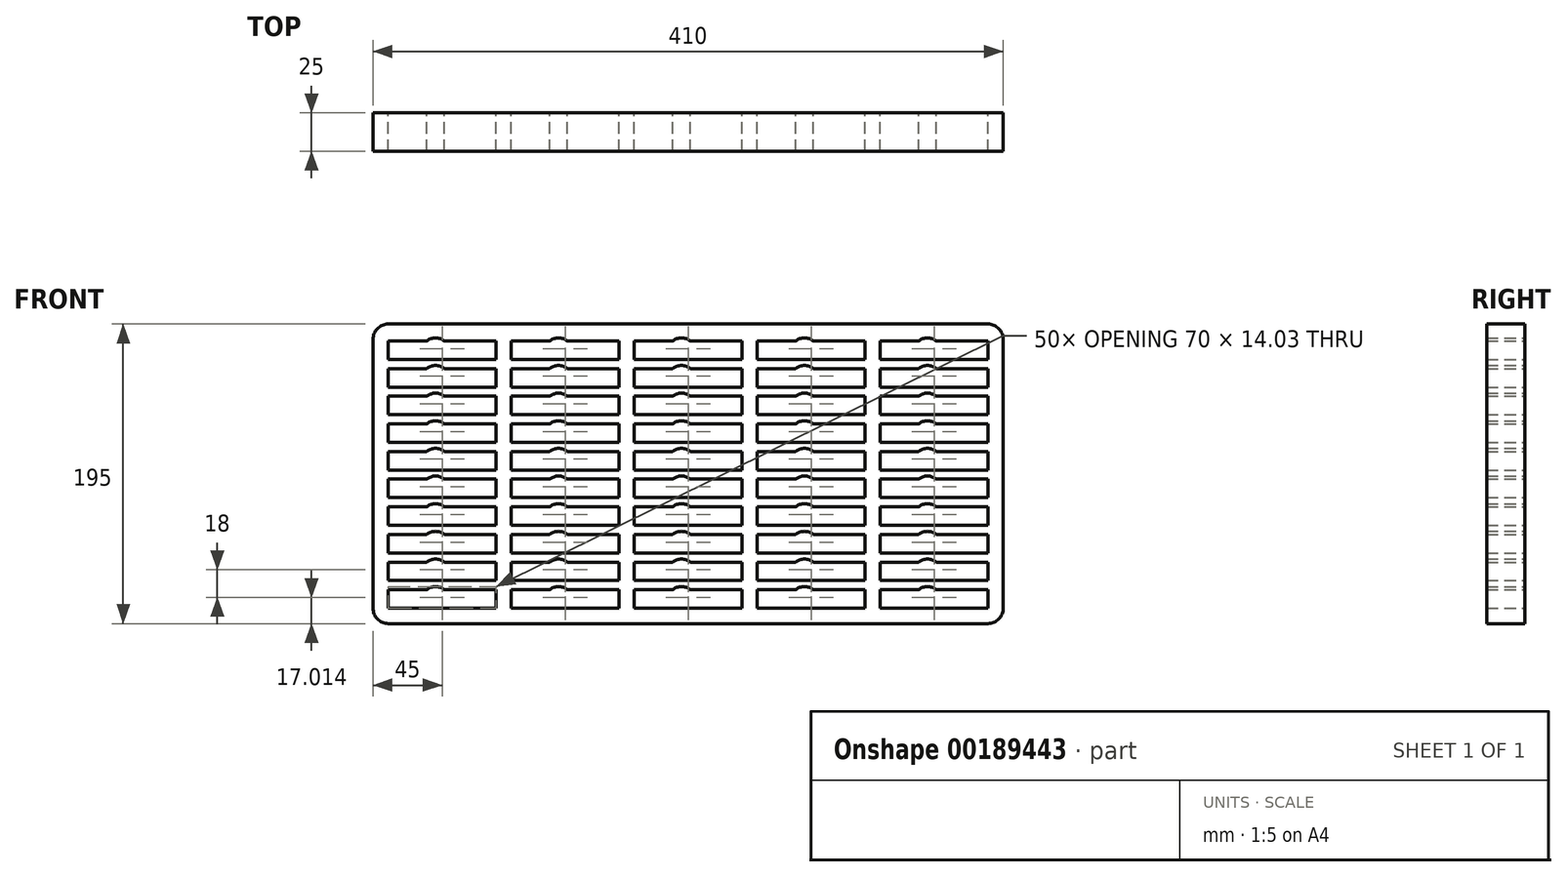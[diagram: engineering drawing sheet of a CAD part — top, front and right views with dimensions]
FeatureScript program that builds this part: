
annotation { "Feature Type Name" : "Feature", "Feature Type Description" : "" }
export const myFeature = defineFeature(function(context is Context, id is Id, definition is map)
    precondition{}
    {
        {
            var Q0;
            Q0=qCreatedBy(makeId("Front.planeOp"),FACE);
            var sketch = newSketch(context, id + "F0", { "sketchPlane" : qUnion([Q0])});
            skLineSegment(sketch, "E0.bottom", {"start": v(10, 0) * mm, "end": v(400, 0) * mm});
            skLineSegment(sketch, "E0.top", {"start": v(10, 195) * mm, "end": v(400, 195) * mm});
            skLineSegment(sketch, "E0.left", {"start": v(0, 10) * mm, "end": v(0, 185) * mm});
            skLineSegment(sketch, "E0.right", {"start": v(410, 10) * mm, "end": v(410, 185) * mm});
            skLineSegment(sketch, "E1.bottom", {"start": v(10, 10) * mm, "end": v(80, 10) * mm});
            skLineSegment(sketch, "E1.top", {"start": v(10, 22) * mm, "end": v(80, 22) * mm});
            skLineSegment(sketch, "E1.left", {"start": v(10, 10) * mm, "end": v(10, 22) * mm});
            skLineSegment(sketch, "E1.right", {"start": v(80, 10) * mm, "end": v(80, 22) * mm});
            skArc(sketch, "E2", {"start": v(46.47, 22) * mm, "mid": v(40.7, 24.03) * mm, "end": v(34.93, 22) * mm});
            skLineSegment(sketch, "E3.0.1.0", {"start": v(10, 28) * mm, "end": v(80, 28) * mm});
            skLineSegment(sketch, "E3.0.1.1", {"start": v(80, 28) * mm, "end": v(80, 40) * mm});
            skLineSegment(sketch, "E3.0.1.2", {"start": v(10, 40) * mm, "end": v(80, 40) * mm});
            skArc(sketch, "E3.0.1.3", {"start": v(46.47, 40) * mm, "mid": v(40.7, 42.03) * mm, "end": v(34.93, 40) * mm});
            skLineSegment(sketch, "E3.0.1.4", {"start": v(10, 28) * mm, "end": v(10, 40) * mm});
            skLineSegment(sketch, "E3.0.2.0", {"start": v(10, 46) * mm, "end": v(80, 46) * mm});
            skLineSegment(sketch, "E3.0.2.1", {"start": v(80, 46) * mm, "end": v(80, 58) * mm});
            skLineSegment(sketch, "E3.0.2.2", {"start": v(10, 58) * mm, "end": v(80, 58) * mm});
            skArc(sketch, "E3.0.2.3", {"start": v(46.47, 58) * mm, "mid": v(40.7, 60.03) * mm, "end": v(34.93, 58) * mm});
            skLineSegment(sketch, "E3.0.2.4", {"start": v(10, 46) * mm, "end": v(10, 58) * mm});
            skLineSegment(sketch, "E3.0.3.0", {"start": v(10, 64) * mm, "end": v(80, 64) * mm});
            skLineSegment(sketch, "E3.0.3.1", {"start": v(80, 64) * mm, "end": v(80, 76) * mm});
            skLineSegment(sketch, "E3.0.3.2", {"start": v(10, 76) * mm, "end": v(80, 76) * mm});
            skArc(sketch, "E3.0.3.3", {"start": v(46.47, 76) * mm, "mid": v(40.7, 78.03) * mm, "end": v(34.93, 76) * mm});
            skLineSegment(sketch, "E3.0.3.4", {"start": v(10, 64) * mm, "end": v(10, 76) * mm});
            skLineSegment(sketch, "E3.0.4.0", {"start": v(10, 82) * mm, "end": v(80, 82) * mm});
            skLineSegment(sketch, "E3.0.4.1", {"start": v(80, 82) * mm, "end": v(80, 94) * mm});
            skLineSegment(sketch, "E3.0.4.2", {"start": v(10, 94) * mm, "end": v(80, 94) * mm});
            skArc(sketch, "E3.0.4.3", {"start": v(46.47, 94) * mm, "mid": v(40.7, 96.03) * mm, "end": v(34.93, 94) * mm});
            skLineSegment(sketch, "E3.0.4.4", {"start": v(10, 82) * mm, "end": v(10, 94) * mm});
            skLineSegment(sketch, "E3.0.5.0", {"start": v(10, 100) * mm, "end": v(80, 100) * mm});
            skLineSegment(sketch, "E3.0.5.1", {"start": v(80, 100) * mm, "end": v(80, 112) * mm});
            skLineSegment(sketch, "E3.0.5.2", {"start": v(10, 112) * mm, "end": v(80, 112) * mm});
            skArc(sketch, "E3.0.5.3", {"start": v(46.47, 112) * mm, "mid": v(40.7, 114.03) * mm, "end": v(34.93, 112) * mm});
            skLineSegment(sketch, "E3.0.5.4", {"start": v(10, 100) * mm, "end": v(10, 112) * mm});
            skLineSegment(sketch, "E3.0.6.0", {"start": v(10, 118) * mm, "end": v(80, 118) * mm});
            skLineSegment(sketch, "E3.0.6.1", {"start": v(80, 118) * mm, "end": v(80, 130) * mm});
            skLineSegment(sketch, "E3.0.6.2", {"start": v(10, 130) * mm, "end": v(80, 130) * mm});
            skArc(sketch, "E3.0.6.3", {"start": v(46.47, 130) * mm, "mid": v(40.7, 132.03) * mm, "end": v(34.93, 130) * mm});
            skLineSegment(sketch, "E3.0.6.4", {"start": v(10, 118) * mm, "end": v(10, 130) * mm});
            skLineSegment(sketch, "E3.0.7.0", {"start": v(10, 136) * mm, "end": v(80, 136) * mm});
            skLineSegment(sketch, "E3.0.7.1", {"start": v(80, 136) * mm, "end": v(80, 148) * mm});
            skLineSegment(sketch, "E3.0.7.2", {"start": v(10, 148) * mm, "end": v(80, 148) * mm});
            skArc(sketch, "E3.0.7.3", {"start": v(46.47, 148) * mm, "mid": v(40.7, 150.03) * mm, "end": v(34.93, 148) * mm});
            skLineSegment(sketch, "E3.0.7.4", {"start": v(10, 136) * mm, "end": v(10, 148) * mm});
            skLineSegment(sketch, "E3.0.8.0", {"start": v(10, 154) * mm, "end": v(80, 154) * mm});
            skLineSegment(sketch, "E3.0.8.1", {"start": v(80, 154) * mm, "end": v(80, 166) * mm});
            skLineSegment(sketch, "E3.0.8.2", {"start": v(10, 166) * mm, "end": v(80, 166) * mm});
            skArc(sketch, "E3.0.8.3", {"start": v(46.47, 166) * mm, "mid": v(40.7, 168.03) * mm, "end": v(34.93, 166) * mm});
            skLineSegment(sketch, "E3.0.8.4", {"start": v(10, 154) * mm, "end": v(10, 166) * mm});
            skLineSegment(sketch, "E3.0.9.0", {"start": v(10, 172) * mm, "end": v(80, 172) * mm});
            skLineSegment(sketch, "E3.0.9.1", {"start": v(80, 172) * mm, "end": v(80, 184) * mm});
            skLineSegment(sketch, "E3.0.9.2", {"start": v(10, 184) * mm, "end": v(80, 184) * mm});
            skArc(sketch, "E3.0.9.3", {"start": v(46.47, 184) * mm, "mid": v(40.7, 186.03) * mm, "end": v(34.93, 184) * mm});
            skLineSegment(sketch, "E3.0.9.4", {"start": v(10, 172) * mm, "end": v(10, 184) * mm});
            skLineSegment(sketch, "E3.1.0.0", {"start": v(90, 10) * mm, "end": v(160, 10) * mm});
            skLineSegment(sketch, "E3.1.0.1", {"start": v(160, 10) * mm, "end": v(160, 22) * mm});
            skLineSegment(sketch, "E3.1.0.2", {"start": v(90, 22) * mm, "end": v(160, 22) * mm});
            skArc(sketch, "E3.1.0.3", {"start": v(126.47, 22) * mm, "mid": v(120.7, 24.03) * mm, "end": v(114.93, 22) * mm});
            skLineSegment(sketch, "E3.1.0.4", {"start": v(90, 10) * mm, "end": v(90, 22) * mm});
            skLineSegment(sketch, "E3.1.1.0", {"start": v(90, 28) * mm, "end": v(160, 28) * mm});
            skLineSegment(sketch, "E3.1.1.1", {"start": v(160, 28) * mm, "end": v(160, 40) * mm});
            skLineSegment(sketch, "E3.1.1.2", {"start": v(90, 40) * mm, "end": v(160, 40) * mm});
            skArc(sketch, "E3.1.1.3", {"start": v(126.47, 40) * mm, "mid": v(120.7, 42.03) * mm, "end": v(114.93, 40) * mm});
            skLineSegment(sketch, "E3.1.1.4", {"start": v(90, 28) * mm, "end": v(90, 40) * mm});
            skLineSegment(sketch, "E3.1.2.0", {"start": v(90, 46) * mm, "end": v(160, 46) * mm});
            skLineSegment(sketch, "E3.1.2.1", {"start": v(160, 46) * mm, "end": v(160, 58) * mm});
            skLineSegment(sketch, "E3.1.2.2", {"start": v(90, 58) * mm, "end": v(160, 58) * mm});
            skArc(sketch, "E3.1.2.3", {"start": v(126.47, 58) * mm, "mid": v(120.7, 60.03) * mm, "end": v(114.93, 58) * mm});
            skLineSegment(sketch, "E3.1.2.4", {"start": v(90, 46) * mm, "end": v(90, 58) * mm});
            skLineSegment(sketch, "E3.1.3.0", {"start": v(90, 64) * mm, "end": v(160, 64) * mm});
            skLineSegment(sketch, "E3.1.3.1", {"start": v(160, 64) * mm, "end": v(160, 76) * mm});
            skLineSegment(sketch, "E3.1.3.2", {"start": v(90, 76) * mm, "end": v(160, 76) * mm});
            skArc(sketch, "E3.1.3.3", {"start": v(126.47, 76) * mm, "mid": v(120.7, 78.03) * mm, "end": v(114.93, 76) * mm});
            skLineSegment(sketch, "E3.1.3.4", {"start": v(90, 64) * mm, "end": v(90, 76) * mm});
            skLineSegment(sketch, "E3.1.4.0", {"start": v(90, 82) * mm, "end": v(160, 82) * mm});
            skLineSegment(sketch, "E3.1.4.1", {"start": v(160, 82) * mm, "end": v(160, 94) * mm});
            skLineSegment(sketch, "E3.1.4.2", {"start": v(90, 94) * mm, "end": v(160, 94) * mm});
            skArc(sketch, "E3.1.4.3", {"start": v(126.47, 94) * mm, "mid": v(120.7, 96.03) * mm, "end": v(114.93, 94) * mm});
            skLineSegment(sketch, "E3.1.4.4", {"start": v(90, 82) * mm, "end": v(90, 94) * mm});
            skLineSegment(sketch, "E3.1.5.0", {"start": v(90, 100) * mm, "end": v(160, 100) * mm});
            skLineSegment(sketch, "E3.1.5.1", {"start": v(160, 100) * mm, "end": v(160, 112) * mm});
            skLineSegment(sketch, "E3.1.5.2", {"start": v(90, 112) * mm, "end": v(160, 112) * mm});
            skArc(sketch, "E3.1.5.3", {"start": v(126.47, 112) * mm, "mid": v(120.7, 114.03) * mm, "end": v(114.93, 112) * mm});
            skLineSegment(sketch, "E3.1.5.4", {"start": v(90, 100) * mm, "end": v(90, 112) * mm});
            skLineSegment(sketch, "E3.1.6.0", {"start": v(90, 118) * mm, "end": v(160, 118) * mm});
            skLineSegment(sketch, "E3.1.6.1", {"start": v(160, 118) * mm, "end": v(160, 130) * mm});
            skLineSegment(sketch, "E3.1.6.2", {"start": v(90, 130) * mm, "end": v(160, 130) * mm});
            skArc(sketch, "E3.1.6.3", {"start": v(126.47, 130) * mm, "mid": v(120.7, 132.03) * mm, "end": v(114.93, 130) * mm});
            skLineSegment(sketch, "E3.1.6.4", {"start": v(90, 118) * mm, "end": v(90, 130) * mm});
            skLineSegment(sketch, "E3.1.7.0", {"start": v(90, 136) * mm, "end": v(160, 136) * mm});
            skLineSegment(sketch, "E3.1.7.1", {"start": v(160, 136) * mm, "end": v(160, 148) * mm});
            skLineSegment(sketch, "E3.1.7.2", {"start": v(90, 148) * mm, "end": v(160, 148) * mm});
            skArc(sketch, "E3.1.7.3", {"start": v(126.47, 148) * mm, "mid": v(120.7, 150.03) * mm, "end": v(114.93, 148) * mm});
            skLineSegment(sketch, "E3.1.7.4", {"start": v(90, 136) * mm, "end": v(90, 148) * mm});
            skLineSegment(sketch, "E3.1.8.0", {"start": v(90, 154) * mm, "end": v(160, 154) * mm});
            skLineSegment(sketch, "E3.1.8.1", {"start": v(160, 154) * mm, "end": v(160, 166) * mm});
            skLineSegment(sketch, "E3.1.8.2", {"start": v(90, 166) * mm, "end": v(160, 166) * mm});
            skArc(sketch, "E3.1.8.3", {"start": v(126.47, 166) * mm, "mid": v(120.7, 168.03) * mm, "end": v(114.93, 166) * mm});
            skLineSegment(sketch, "E3.1.8.4", {"start": v(90, 154) * mm, "end": v(90, 166) * mm});
            skLineSegment(sketch, "E3.1.9.0", {"start": v(90, 172) * mm, "end": v(160, 172) * mm});
            skLineSegment(sketch, "E3.1.9.1", {"start": v(160, 172) * mm, "end": v(160, 184) * mm});
            skLineSegment(sketch, "E3.1.9.2", {"start": v(90, 184) * mm, "end": v(160, 184) * mm});
            skArc(sketch, "E3.1.9.3", {"start": v(126.47, 184) * mm, "mid": v(120.7, 186.03) * mm, "end": v(114.93, 184) * mm});
            skLineSegment(sketch, "E3.1.9.4", {"start": v(90, 172) * mm, "end": v(90, 184) * mm});
            skLineSegment(sketch, "E3.2.0.0", {"start": v(170, 10) * mm, "end": v(240, 10) * mm});
            skLineSegment(sketch, "E3.2.0.1", {"start": v(240, 10) * mm, "end": v(240, 22) * mm});
            skLineSegment(sketch, "E3.2.0.2", {"start": v(170, 22) * mm, "end": v(240, 22) * mm});
            skArc(sketch, "E3.2.0.3", {"start": v(206.47, 22) * mm, "mid": v(200.7, 24.03) * mm, "end": v(194.93, 22) * mm});
            skLineSegment(sketch, "E3.2.0.4", {"start": v(170, 10) * mm, "end": v(170, 22) * mm});
            skLineSegment(sketch, "E3.2.1.0", {"start": v(170, 28) * mm, "end": v(240, 28) * mm});
            skLineSegment(sketch, "E3.2.1.1", {"start": v(240, 28) * mm, "end": v(240, 40) * mm});
            skLineSegment(sketch, "E3.2.1.2", {"start": v(170, 40) * mm, "end": v(240, 40) * mm});
            skArc(sketch, "E3.2.1.3", {"start": v(206.47, 40) * mm, "mid": v(200.7, 42.03) * mm, "end": v(194.93, 40) * mm});
            skLineSegment(sketch, "E3.2.1.4", {"start": v(170, 28) * mm, "end": v(170, 40) * mm});
            skLineSegment(sketch, "E3.2.2.0", {"start": v(170, 46) * mm, "end": v(240, 46) * mm});
            skLineSegment(sketch, "E3.2.2.1", {"start": v(240, 46) * mm, "end": v(240, 58) * mm});
            skLineSegment(sketch, "E3.2.2.2", {"start": v(170, 58) * mm, "end": v(240, 58) * mm});
            skArc(sketch, "E3.2.2.3", {"start": v(206.47, 58) * mm, "mid": v(200.7, 60.03) * mm, "end": v(194.93, 58) * mm});
            skLineSegment(sketch, "E3.2.2.4", {"start": v(170, 46) * mm, "end": v(170, 58) * mm});
            skLineSegment(sketch, "E3.2.3.0", {"start": v(170, 64) * mm, "end": v(240, 64) * mm});
            skLineSegment(sketch, "E3.2.3.1", {"start": v(240, 64) * mm, "end": v(240, 76) * mm});
            skLineSegment(sketch, "E3.2.3.2", {"start": v(170, 76) * mm, "end": v(240, 76) * mm});
            skArc(sketch, "E3.2.3.3", {"start": v(206.47, 76) * mm, "mid": v(200.7, 78.03) * mm, "end": v(194.93, 76) * mm});
            skLineSegment(sketch, "E3.2.3.4", {"start": v(170, 64) * mm, "end": v(170, 76) * mm});
            skLineSegment(sketch, "E3.2.4.0", {"start": v(170, 82) * mm, "end": v(240, 82) * mm});
            skLineSegment(sketch, "E3.2.4.1", {"start": v(240, 82) * mm, "end": v(240, 94) * mm});
            skLineSegment(sketch, "E3.2.4.2", {"start": v(170, 94) * mm, "end": v(240, 94) * mm});
            skArc(sketch, "E3.2.4.3", {"start": v(206.47, 94) * mm, "mid": v(200.7, 96.03) * mm, "end": v(194.93, 94) * mm});
            skLineSegment(sketch, "E3.2.4.4", {"start": v(170, 82) * mm, "end": v(170, 94) * mm});
            skLineSegment(sketch, "E3.2.5.0", {"start": v(170, 100) * mm, "end": v(240, 100) * mm});
            skLineSegment(sketch, "E3.2.5.1", {"start": v(240, 100) * mm, "end": v(240, 112) * mm});
            skLineSegment(sketch, "E3.2.5.2", {"start": v(170, 112) * mm, "end": v(240, 112) * mm});
            skArc(sketch, "E3.2.5.3", {"start": v(206.47, 112) * mm, "mid": v(200.7, 114.03) * mm, "end": v(194.93, 112) * mm});
            skLineSegment(sketch, "E3.2.5.4", {"start": v(170, 100) * mm, "end": v(170, 112) * mm});
            skLineSegment(sketch, "E3.2.6.0", {"start": v(170, 118) * mm, "end": v(240, 118) * mm});
            skLineSegment(sketch, "E3.2.6.1", {"start": v(240, 118) * mm, "end": v(240, 130) * mm});
            skLineSegment(sketch, "E3.2.6.2", {"start": v(170, 130) * mm, "end": v(240, 130) * mm});
            skArc(sketch, "E3.2.6.3", {"start": v(206.47, 130) * mm, "mid": v(200.7, 132.03) * mm, "end": v(194.93, 130) * mm});
            skLineSegment(sketch, "E3.2.6.4", {"start": v(170, 118) * mm, "end": v(170, 130) * mm});
            skLineSegment(sketch, "E3.2.7.0", {"start": v(170, 136) * mm, "end": v(240, 136) * mm});
            skLineSegment(sketch, "E3.2.7.1", {"start": v(240, 136) * mm, "end": v(240, 148) * mm});
            skLineSegment(sketch, "E3.2.7.2", {"start": v(170, 148) * mm, "end": v(240, 148) * mm});
            skArc(sketch, "E3.2.7.3", {"start": v(206.47, 148) * mm, "mid": v(200.7, 150.03) * mm, "end": v(194.93, 148) * mm});
            skLineSegment(sketch, "E3.2.7.4", {"start": v(170, 136) * mm, "end": v(170, 148) * mm});
            skLineSegment(sketch, "E3.2.8.0", {"start": v(170, 154) * mm, "end": v(240, 154) * mm});
            skLineSegment(sketch, "E3.2.8.1", {"start": v(240, 154) * mm, "end": v(240, 166) * mm});
            skLineSegment(sketch, "E3.2.8.2", {"start": v(170, 166) * mm, "end": v(240, 166) * mm});
            skArc(sketch, "E3.2.8.3", {"start": v(206.47, 166) * mm, "mid": v(200.7, 168.03) * mm, "end": v(194.93, 166) * mm});
            skLineSegment(sketch, "E3.2.8.4", {"start": v(170, 154) * mm, "end": v(170, 166) * mm});
            skLineSegment(sketch, "E3.2.9.0", {"start": v(170, 172) * mm, "end": v(240, 172) * mm});
            skLineSegment(sketch, "E3.2.9.1", {"start": v(240, 172) * mm, "end": v(240, 184) * mm});
            skLineSegment(sketch, "E3.2.9.2", {"start": v(170, 184) * mm, "end": v(240, 184) * mm});
            skArc(sketch, "E3.2.9.3", {"start": v(206.47, 184) * mm, "mid": v(200.7, 186.03) * mm, "end": v(194.93, 184) * mm});
            skLineSegment(sketch, "E3.2.9.4", {"start": v(170, 172) * mm, "end": v(170, 184) * mm});
            skLineSegment(sketch, "E3.3.0.0", {"start": v(250, 10) * mm, "end": v(320, 10) * mm});
            skLineSegment(sketch, "E3.3.0.1", {"start": v(320, 10) * mm, "end": v(320, 22) * mm});
            skLineSegment(sketch, "E3.3.0.2", {"start": v(250, 22) * mm, "end": v(320, 22) * mm});
            skArc(sketch, "E3.3.0.3", {"start": v(286.47, 22) * mm, "mid": v(280.7, 24.03) * mm, "end": v(274.93, 22) * mm});
            skLineSegment(sketch, "E3.3.0.4", {"start": v(250, 10) * mm, "end": v(250, 22) * mm});
            skLineSegment(sketch, "E3.3.1.0", {"start": v(250, 28) * mm, "end": v(320, 28) * mm});
            skLineSegment(sketch, "E3.3.1.1", {"start": v(320, 28) * mm, "end": v(320, 40) * mm});
            skLineSegment(sketch, "E3.3.1.2", {"start": v(250, 40) * mm, "end": v(320, 40) * mm});
            skArc(sketch, "E3.3.1.3", {"start": v(286.47, 40) * mm, "mid": v(280.7, 42.03) * mm, "end": v(274.93, 40) * mm});
            skLineSegment(sketch, "E3.3.1.4", {"start": v(250, 28) * mm, "end": v(250, 40) * mm});
            skLineSegment(sketch, "E3.3.2.0", {"start": v(250, 46) * mm, "end": v(320, 46) * mm});
            skLineSegment(sketch, "E3.3.2.1", {"start": v(320, 46) * mm, "end": v(320, 58) * mm});
            skLineSegment(sketch, "E3.3.2.2", {"start": v(250, 58) * mm, "end": v(320, 58) * mm});
            skArc(sketch, "E3.3.2.3", {"start": v(286.47, 58) * mm, "mid": v(280.7, 60.03) * mm, "end": v(274.93, 58) * mm});
            skLineSegment(sketch, "E3.3.2.4", {"start": v(250, 46) * mm, "end": v(250, 58) * mm});
            skLineSegment(sketch, "E3.3.3.0", {"start": v(250, 64) * mm, "end": v(320, 64) * mm});
            skLineSegment(sketch, "E3.3.3.1", {"start": v(320, 64) * mm, "end": v(320, 76) * mm});
            skLineSegment(sketch, "E3.3.3.2", {"start": v(250, 76) * mm, "end": v(320, 76) * mm});
            skArc(sketch, "E3.3.3.3", {"start": v(286.47, 76) * mm, "mid": v(280.7, 78.03) * mm, "end": v(274.93, 76) * mm});
            skLineSegment(sketch, "E3.3.3.4", {"start": v(250, 64) * mm, "end": v(250, 76) * mm});
            skLineSegment(sketch, "E3.3.4.0", {"start": v(250, 82) * mm, "end": v(320, 82) * mm});
            skLineSegment(sketch, "E3.3.4.1", {"start": v(320, 82) * mm, "end": v(320, 94) * mm});
            skLineSegment(sketch, "E3.3.4.2", {"start": v(250, 94) * mm, "end": v(320, 94) * mm});
            skArc(sketch, "E3.3.4.3", {"start": v(286.47, 94) * mm, "mid": v(280.7, 96.03) * mm, "end": v(274.93, 94) * mm});
            skLineSegment(sketch, "E3.3.4.4", {"start": v(250, 82) * mm, "end": v(250, 94) * mm});
            skLineSegment(sketch, "E3.3.5.0", {"start": v(250, 100) * mm, "end": v(320, 100) * mm});
            skLineSegment(sketch, "E3.3.5.1", {"start": v(320, 100) * mm, "end": v(320, 112) * mm});
            skLineSegment(sketch, "E3.3.5.2", {"start": v(250, 112) * mm, "end": v(320, 112) * mm});
            skArc(sketch, "E3.3.5.3", {"start": v(286.47, 112) * mm, "mid": v(280.7, 114.03) * mm, "end": v(274.93, 112) * mm});
            skLineSegment(sketch, "E3.3.5.4", {"start": v(250, 100) * mm, "end": v(250, 112) * mm});
            skLineSegment(sketch, "E3.3.6.0", {"start": v(250, 118) * mm, "end": v(320, 118) * mm});
            skLineSegment(sketch, "E3.3.6.1", {"start": v(320, 118) * mm, "end": v(320, 130) * mm});
            skLineSegment(sketch, "E3.3.6.2", {"start": v(250, 130) * mm, "end": v(320, 130) * mm});
            skArc(sketch, "E3.3.6.3", {"start": v(286.47, 130) * mm, "mid": v(280.7, 132.03) * mm, "end": v(274.93, 130) * mm});
            skLineSegment(sketch, "E3.3.6.4", {"start": v(250, 118) * mm, "end": v(250, 130) * mm});
            skLineSegment(sketch, "E3.3.7.0", {"start": v(250, 136) * mm, "end": v(320, 136) * mm});
            skLineSegment(sketch, "E3.3.7.1", {"start": v(320, 136) * mm, "end": v(320, 148) * mm});
            skLineSegment(sketch, "E3.3.7.2", {"start": v(250, 148) * mm, "end": v(320, 148) * mm});
            skArc(sketch, "E3.3.7.3", {"start": v(286.47, 148) * mm, "mid": v(280.7, 150.03) * mm, "end": v(274.93, 148) * mm});
            skLineSegment(sketch, "E3.3.7.4", {"start": v(250, 136) * mm, "end": v(250, 148) * mm});
            skLineSegment(sketch, "E3.3.8.0", {"start": v(250, 154) * mm, "end": v(320, 154) * mm});
            skLineSegment(sketch, "E3.3.8.1", {"start": v(320, 154) * mm, "end": v(320, 166) * mm});
            skLineSegment(sketch, "E3.3.8.2", {"start": v(250, 166) * mm, "end": v(320, 166) * mm});
            skArc(sketch, "E3.3.8.3", {"start": v(286.47, 166) * mm, "mid": v(280.7, 168.03) * mm, "end": v(274.93, 166) * mm});
            skLineSegment(sketch, "E3.3.8.4", {"start": v(250, 154) * mm, "end": v(250, 166) * mm});
            skLineSegment(sketch, "E3.3.9.0", {"start": v(250, 172) * mm, "end": v(320, 172) * mm});
            skLineSegment(sketch, "E3.3.9.1", {"start": v(320, 172) * mm, "end": v(320, 184) * mm});
            skLineSegment(sketch, "E3.3.9.2", {"start": v(250, 184) * mm, "end": v(320, 184) * mm});
            skArc(sketch, "E3.3.9.3", {"start": v(286.47, 184) * mm, "mid": v(280.7, 186.03) * mm, "end": v(274.93, 184) * mm});
            skLineSegment(sketch, "E3.3.9.4", {"start": v(250, 172) * mm, "end": v(250, 184) * mm});
            skLineSegment(sketch, "E3.4.0.0", {"start": v(330, 10) * mm, "end": v(400, 10) * mm});
            skLineSegment(sketch, "E3.4.0.1", {"start": v(400, 10) * mm, "end": v(400, 22) * mm});
            skLineSegment(sketch, "E3.4.0.2", {"start": v(330, 22) * mm, "end": v(400, 22) * mm});
            skArc(sketch, "E3.4.0.3", {"start": v(366.47, 22) * mm, "mid": v(360.7, 24.03) * mm, "end": v(354.93, 22) * mm});
            skLineSegment(sketch, "E3.4.0.4", {"start": v(330, 10) * mm, "end": v(330, 22) * mm});
            skLineSegment(sketch, "E3.4.1.0", {"start": v(330, 28) * mm, "end": v(400, 28) * mm});
            skLineSegment(sketch, "E3.4.1.1", {"start": v(400, 28) * mm, "end": v(400, 40) * mm});
            skLineSegment(sketch, "E3.4.1.2", {"start": v(330, 40) * mm, "end": v(400, 40) * mm});
            skArc(sketch, "E3.4.1.3", {"start": v(366.47, 40) * mm, "mid": v(360.7, 42.03) * mm, "end": v(354.93, 40) * mm});
            skLineSegment(sketch, "E3.4.1.4", {"start": v(330, 28) * mm, "end": v(330, 40) * mm});
            skLineSegment(sketch, "E3.4.2.0", {"start": v(330, 46) * mm, "end": v(400, 46) * mm});
            skLineSegment(sketch, "E3.4.2.1", {"start": v(400, 46) * mm, "end": v(400, 58) * mm});
            skLineSegment(sketch, "E3.4.2.2", {"start": v(330, 58) * mm, "end": v(400, 58) * mm});
            skArc(sketch, "E3.4.2.3", {"start": v(366.47, 58) * mm, "mid": v(360.7, 60.03) * mm, "end": v(354.93, 58) * mm});
            skLineSegment(sketch, "E3.4.2.4", {"start": v(330, 46) * mm, "end": v(330, 58) * mm});
            skLineSegment(sketch, "E3.4.3.0", {"start": v(330, 64) * mm, "end": v(400, 64) * mm});
            skLineSegment(sketch, "E3.4.3.1", {"start": v(400, 64) * mm, "end": v(400, 76) * mm});
            skLineSegment(sketch, "E3.4.3.2", {"start": v(330, 76) * mm, "end": v(400, 76) * mm});
            skArc(sketch, "E3.4.3.3", {"start": v(366.47, 76) * mm, "mid": v(360.7, 78.03) * mm, "end": v(354.93, 76) * mm});
            skLineSegment(sketch, "E3.4.3.4", {"start": v(330, 64) * mm, "end": v(330, 76) * mm});
            skLineSegment(sketch, "E3.4.4.0", {"start": v(330, 82) * mm, "end": v(400, 82) * mm});
            skLineSegment(sketch, "E3.4.4.1", {"start": v(400, 82) * mm, "end": v(400, 94) * mm});
            skLineSegment(sketch, "E3.4.4.2", {"start": v(330, 94) * mm, "end": v(400, 94) * mm});
            skArc(sketch, "E3.4.4.3", {"start": v(366.47, 94) * mm, "mid": v(360.7, 96.03) * mm, "end": v(354.93, 94) * mm});
            skLineSegment(sketch, "E3.4.4.4", {"start": v(330, 82) * mm, "end": v(330, 94) * mm});
            skLineSegment(sketch, "E3.4.5.0", {"start": v(330, 100) * mm, "end": v(400, 100) * mm});
            skLineSegment(sketch, "E3.4.5.1", {"start": v(400, 100) * mm, "end": v(400, 112) * mm});
            skLineSegment(sketch, "E3.4.5.2", {"start": v(330, 112) * mm, "end": v(400, 112) * mm});
            skArc(sketch, "E3.4.5.3", {"start": v(366.47, 112) * mm, "mid": v(360.7, 114.03) * mm, "end": v(354.93, 112) * mm});
            skLineSegment(sketch, "E3.4.5.4", {"start": v(330, 100) * mm, "end": v(330, 112) * mm});
            skLineSegment(sketch, "E3.4.6.0", {"start": v(330, 118) * mm, "end": v(400, 118) * mm});
            skLineSegment(sketch, "E3.4.6.1", {"start": v(400, 118) * mm, "end": v(400, 130) * mm});
            skLineSegment(sketch, "E3.4.6.2", {"start": v(330, 130) * mm, "end": v(400, 130) * mm});
            skArc(sketch, "E3.4.6.3", {"start": v(366.47, 130) * mm, "mid": v(360.7, 132.03) * mm, "end": v(354.93, 130) * mm});
            skLineSegment(sketch, "E3.4.6.4", {"start": v(330, 118) * mm, "end": v(330, 130) * mm});
            skLineSegment(sketch, "E3.4.7.0", {"start": v(330, 136) * mm, "end": v(400, 136) * mm});
            skLineSegment(sketch, "E3.4.7.1", {"start": v(400, 136) * mm, "end": v(400, 148) * mm});
            skLineSegment(sketch, "E3.4.7.2", {"start": v(330, 148) * mm, "end": v(400, 148) * mm});
            skArc(sketch, "E3.4.7.3", {"start": v(366.47, 148) * mm, "mid": v(360.7, 150.03) * mm, "end": v(354.93, 148) * mm});
            skLineSegment(sketch, "E3.4.7.4", {"start": v(330, 136) * mm, "end": v(330, 148) * mm});
            skLineSegment(sketch, "E3.4.8.0", {"start": v(330, 154) * mm, "end": v(400, 154) * mm});
            skLineSegment(sketch, "E3.4.8.1", {"start": v(400, 154) * mm, "end": v(400, 166) * mm});
            skLineSegment(sketch, "E3.4.8.2", {"start": v(330, 166) * mm, "end": v(400, 166) * mm});
            skArc(sketch, "E3.4.8.3", {"start": v(366.47, 166) * mm, "mid": v(360.7, 168.03) * mm, "end": v(354.93, 166) * mm});
            skLineSegment(sketch, "E3.4.8.4", {"start": v(330, 154) * mm, "end": v(330, 166) * mm});
            skLineSegment(sketch, "E3.4.9.0", {"start": v(330, 172) * mm, "end": v(400, 172) * mm});
            skLineSegment(sketch, "E3.4.9.1", {"start": v(400, 172) * mm, "end": v(400, 184) * mm});
            skLineSegment(sketch, "E3.4.9.2", {"start": v(330, 184) * mm, "end": v(400, 184) * mm});
            skArc(sketch, "E3.4.9.3", {"start": v(366.47, 184) * mm, "mid": v(360.7, 186.03) * mm, "end": v(354.93, 184) * mm});
            skLineSegment(sketch, "E3.4.9.4", {"start": v(330, 172) * mm, "end": v(330, 184) * mm});
            skLineSegment(sketch, "E3.direction1", {"start": v(10, 10) * mm, "end": v(90, 10) * mm, "construction": true});
            skLineSegment(sketch, "E3.direction2", {"start": v(10, 10) * mm, "end": v(10, 28) * mm, "construction": true});
            skPoint(sketch, "E4.visualSharp", {"position": v(0, 195) * mm});
            skArc(sketch, "E4.filletArc", {"start": v(10, 195) * mm, "mid": v(2.93, 192.07) * mm, "end": v(0, 185) * mm});
            skPoint(sketch, "E5.visualSharp", {"position": v(410, 0) * mm});
            skArc(sketch, "E5.filletArc", {"start": v(400, 0) * mm, "mid": v(407.07, 2.93) * mm, "end": v(410, 10) * mm});
            skPoint(sketch, "E6.visualSharp", {"position": v(0, 0) * mm});
            skArc(sketch, "E6.filletArc", {"start": v(0, 10) * mm, "mid": v(2.93, 2.93) * mm, "end": v(10, 0) * mm});
            skPoint(sketch, "E7.visualSharp", {"position": v(410, 195) * mm});
            skArc(sketch, "E7.filletArc", {"start": v(410, 185) * mm, "mid": v(407.07, 192.07) * mm, "end": v(400, 195) * mm});
            skSolve(sketch);
        }
        {
            var Q0;
            Q0 = qSketchRegion(id + "F0", true);
            extrude(context, id + "F1", {"entities" : qUnion([Q0]), "depth" : 25 * mm});
        }
    });
